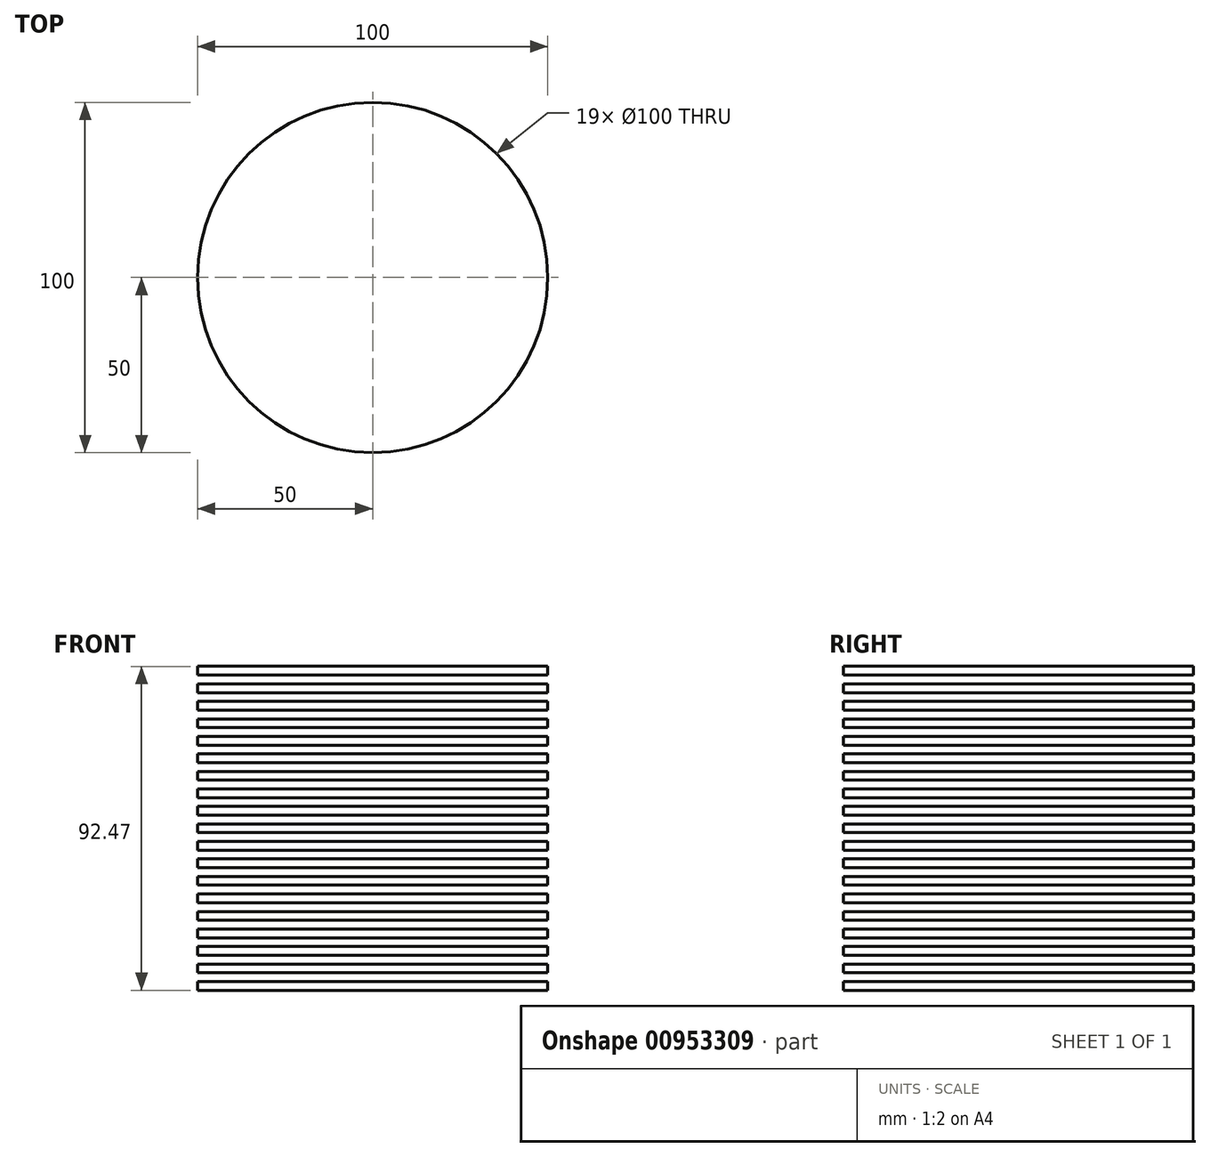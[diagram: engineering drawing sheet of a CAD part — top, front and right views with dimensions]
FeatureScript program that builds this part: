
annotation { "Feature Type Name" : "Feature", "Feature Type Description" : "" }
export const myFeature = defineFeature(function(context is Context, id is Id, definition is map)
    precondition{}
    {
        {
            var Q0;
            Q0=qCreatedBy(makeId("Front.planeOp"),FACE);
            var sketch = newSketch(context, id + "F0", { "sketchPlane" : qUnion([Q0])});
            skLineSegment(sketch, "E0", {"start": v(50, 20) * mm, "end": v(50, 17.5) * mm});
            skLineSegment(sketch, "E1", {"start": v(50, 15) * mm, "end": v(50, 12.5) * mm});
            skLineSegment(sketch, "E2", {"start": v(50, 10) * mm, "end": v(50, 7.5) * mm});
            skLineSegment(sketch, "E3", {"start": v(50, 5) * mm, "end": v(50, 2.5) * mm});
            skLineSegment(sketch, "E4", {"start": v(50, 40) * mm, "end": v(50, 37.5) * mm});
            skLineSegment(sketch, "E5", {"start": v(50, 35) * mm, "end": v(50, 32.5) * mm});
            skLineSegment(sketch, "E6", {"start": v(50, 30) * mm, "end": v(50, 27.5) * mm});
            skLineSegment(sketch, "E7", {"start": v(50, 25) * mm, "end": v(50, 22.5) * mm});
            skLineSegment(sketch, "E8", {"start": v(50, 59.99) * mm, "end": v(50, 57.49) * mm});
            skLineSegment(sketch, "E9", {"start": v(50, 54.99) * mm, "end": v(50, 52.49) * mm});
            skLineSegment(sketch, "E10", {"start": v(50, 49.99) * mm, "end": v(50, 47.49) * mm});
            skLineSegment(sketch, "E11", {"start": v(50, 44.99) * mm, "end": v(50, 42.5) * mm});
            skLineSegment(sketch, "E12", {"start": v(50, 79.98) * mm, "end": v(50, 77.48) * mm});
            skLineSegment(sketch, "E13", {"start": v(50, 74.98) * mm, "end": v(50, 72.48) * mm});
            skLineSegment(sketch, "E14", {"start": v(50, 69.98) * mm, "end": v(50, 67.48) * mm});
            skLineSegment(sketch, "E15", {"start": v(50, 64.98) * mm, "end": v(50, 62.49) * mm});
            skLineSegment(sketch, "E16", {"start": v(50, 94.97) * mm, "end": v(50, 92.47) * mm});
            skLineSegment(sketch, "E17", {"start": v(50, 89.97) * mm, "end": v(50, 87.47) * mm});
            skLineSegment(sketch, "E18", {"start": v(50, 84.97) * mm, "end": v(50, 82.48) * mm});
            skLineSegment(sketch, "E19.left", {"start": v(50, 64.98) * mm, "end": v(50, 62.74) * mm});
            skLineSegment(sketch, "E20", {"start": v(0, 4.42) * mm, "end": v(0, 0) * mm});
            skSolve(sketch);
        }
        {
            var Q0;
            Q0=sQuery(id+"F0.wireOp",EDGE,"E16");
            var Q1;
            Q1=sQuery(id+"F0.wireOp",EDGE,"E17");
            var Q2;
            Q2=sQuery(id+"F0.wireOp",EDGE,"E18");
            var Q3;
            Q3=sQuery(id+"F0.wireOp",EDGE,"E12");
            var Q4;
            Q4=sQuery(id+"F0.wireOp",EDGE,"E13");
            var Q5;
            Q5=sQuery(id+"F0.wireOp",EDGE,"E14");
            var Q6;
            Q6=sQuery(id+"F0.wireOp",EDGE,"E15");
            var Q7;
            Q7=sQuery(id+"F0.wireOp",EDGE,"E8");
            var Q8;
            Q8=sQuery(id+"F0.wireOp",EDGE,"E9");
            var Q9;
            Q9=sQuery(id+"F0.wireOp",EDGE,"E10");
            var Q10;
            Q10=sQuery(id+"F0.wireOp",EDGE,"E11");
            var Q11;
            Q11=sQuery(id+"F0.wireOp",EDGE,"E4");
            var Q12;
            Q12=sQuery(id+"F0.wireOp",EDGE,"E5");
            var Q13;
            Q13=sQuery(id+"F0.wireOp",EDGE,"E6");
            var Q14;
            Q14=sQuery(id+"F0.wireOp",EDGE,"E7");
            var Q15;
            Q15=sQuery(id+"F0.wireOp",EDGE,"E0");
            var Q16;
            Q16=sQuery(id+"F0.wireOp",EDGE,"E1");
            var Q17;
            Q17=sQuery(id+"F0.wireOp",EDGE,"E2");
            var Q18;
            Q18=sQuery(id+"F0.wireOp",EDGE,"E3");
            var Q19;
            Q19=sQuery(id+"F0.wireOp",EDGE,"E20");
            revolve(context, id + "F1", {"bodyType" : ToolBodyType.SURFACE, "surfaceOperationType" : NewSurfaceOperationType.NEW, "surfaceEntities" : qUnion([Q0, Q1, Q2, Q3, Q4, Q5, Q6, Q7, Q8, Q9, Q10, Q11, Q12, Q13, Q14, Q15, Q16, Q17, Q18]), "axis" : qUnion([Q19]), "revolveType" : RevolveType.FULL});
        }
    });
